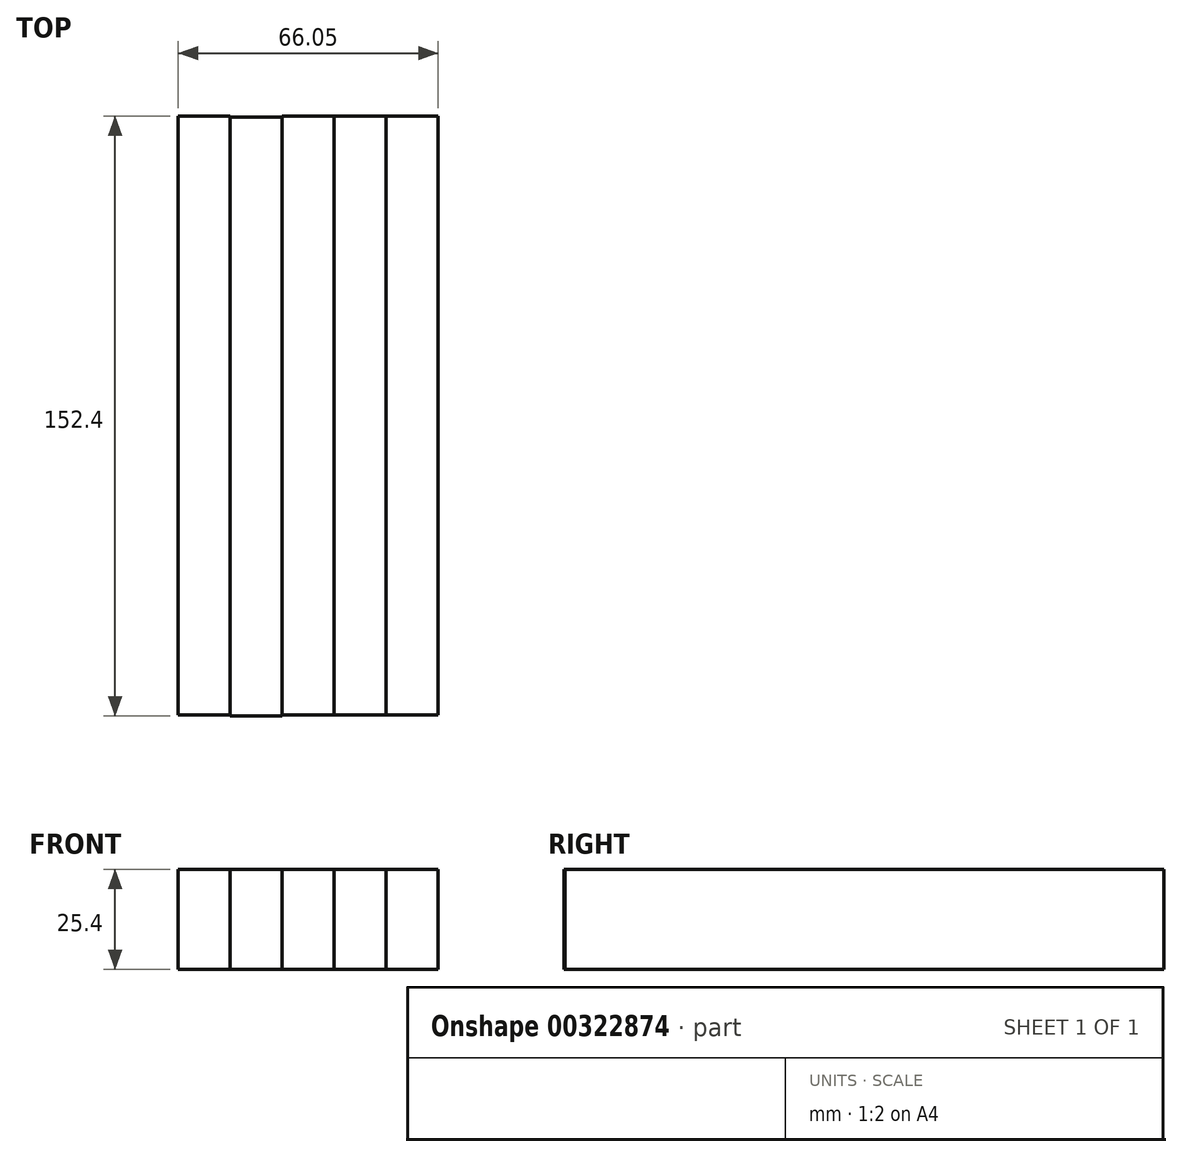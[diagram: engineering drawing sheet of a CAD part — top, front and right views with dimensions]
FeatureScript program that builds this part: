
annotation { "Feature Type Name" : "Feature", "Feature Type Description" : "" }
export const myFeature = defineFeature(function(context is Context, id is Id, definition is map)
    precondition{}
    {
        {
            var Q0;
            Q0=qCreatedBy(makeId("Top.planeOp"),FACE);
            var sketch = newSketch(context, id + "F0", { "sketchPlane" : qUnion([Q0])});
            skLineSegment(sketch, "E0.bottom", {"start": v(-76.5, 76.07) * mm, "end": v(-63.28, 76.07) * mm});
            skLineSegment(sketch, "E0.top", {"start": v(-76.5, -76.07) * mm, "end": v(-63.28, -76.07) * mm});
            skLineSegment(sketch, "E0.left", {"start": v(-76.5, 76.07) * mm, "end": v(-76.5, -76.07) * mm});
            skLineSegment(sketch, "E0.right", {"start": v(-63.28, 76.07) * mm, "end": v(-63.28, -76.07) * mm});
            skSolve(sketch);
        }
        {
            var Q0;
            Q0=makeQuery(id+"F0.imprint","IMPRINT",FACE,{"disambiguationData":[TD([[makeQuery(id+"F0.imprint","IMPRINT",EDGE,{"derivedFrom":sQuery(id+"F0.wireOp",EDGE,"E0.bottom")}),-1.0]])]});
            extrude(context, id + "F1", {"entities" : qUnion([Q0]), "depth" : 25.4 * mm});
        }
        {
            var Q0;
            Q0=makeQuery(id+"F1.opExtrude","SWEPT_BODY",BODY,{"disambiguationData":[OSD([sQuery(id+"F0.wireOp",EDGE,"E0.bottom"),sQuery(id+"F0.wireOp",EDGE,"E0.top"),sQuery(id+"F0.wireOp",EDGE,"E0.left"),sQuery(id+"F0.wireOp",EDGE,"E0.right")])]});
            transform(context, id + "F2", {"entities" : qUnion([Q0]), "transformType" : TransformType.TRANSLATION_3D, "dx" : 13.2 * mm, "dy" : -0.25 * mm, "dz" : 0 * mm, "makeCopy" : true});
        }
        {
            var Q0;
            Q0=makeQuery(id+"F1.opExtrude","SWEPT_BODY",BODY,{"disambiguationData":[OSD([sQuery(id+"F0.wireOp",EDGE,"E0.bottom"),sQuery(id+"F0.wireOp",EDGE,"E0.top"),sQuery(id+"F0.wireOp",EDGE,"E0.left"),sQuery(id+"F0.wireOp",EDGE,"E0.right")])]});
            transform(context, id + "F3", {"entities" : qUnion([Q0]), "transformType" : TransformType.TRANSLATION_3D, "dx" : 26.42 * mm, "dy" : 0 * mm, "dz" : 0 * mm, "makeCopy" : true});
        }
        {
            var Q0;
            Q0=makeQuery(id+"F1.opExtrude","SWEPT_BODY",BODY,{"disambiguationData":[OSD([sQuery(id+"F0.wireOp",EDGE,"E0.bottom"),sQuery(id+"F0.wireOp",EDGE,"E0.top"),sQuery(id+"F0.wireOp",EDGE,"E0.left"),sQuery(id+"F0.wireOp",EDGE,"E0.right")])]});
            transform(context, id + "F4", {"entities" : qUnion([Q0]), "transformType" : TransformType.TRANSLATION_3D, "dx" : 39.62 * mm, "dy" : 0 * mm, "dz" : 0 * mm, "makeCopy" : true});
        }
        {
            var Q0;
            Q0=makeQuery(id+"F1.opExtrude","SWEPT_BODY",BODY,{"disambiguationData":[OSD([sQuery(id+"F0.wireOp",EDGE,"E0.bottom"),sQuery(id+"F0.wireOp",EDGE,"E0.top"),sQuery(id+"F0.wireOp",EDGE,"E0.left"),sQuery(id+"F0.wireOp",EDGE,"E0.right")])]});
            transform(context, id + "F5", {"entities" : qUnion([Q0]), "transformType" : TransformType.TRANSLATION_3D, "dx" : 52.83 * mm, "dy" : 0 * mm, "dz" : 0 * mm, "makeCopy" : true});
        }
    });
